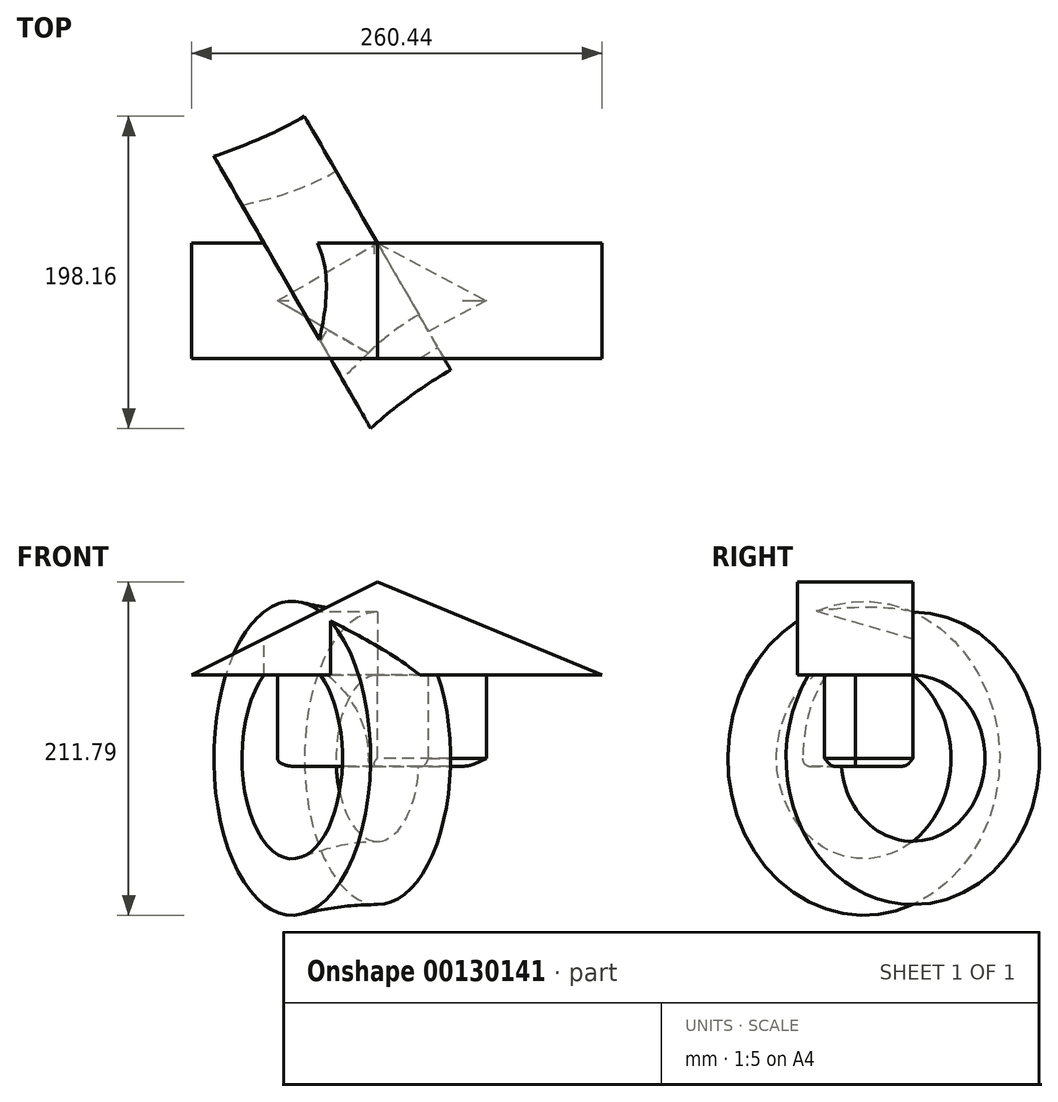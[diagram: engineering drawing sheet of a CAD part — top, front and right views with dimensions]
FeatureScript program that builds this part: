
annotation { "Feature Type Name" : "Feature", "Feature Type Description" : "" }
export const myFeature = defineFeature(function(context is Context, id is Id, definition is map)
    precondition{}
    {
        {
            var Q0;
            Q0=qCreatedBy(makeId("Front.planeOp"),FACE);
            var sketch = newSketch(context, id + "F0", { "sketchPlane" : qUnion([Q0])});
            skLineSegment(sketch, "E0", {"start": v(-118.02, 0) * mm, "end": v(0, 59.3) * mm});
            skLineSegment(sketch, "E1", {"start": v(0, 59.3) * mm, "end": v(142.42, 0) * mm});
            skLineSegment(sketch, "E2", {"start": v(142.42, 0) * mm, "end": v(-118.02, 0) * mm});
            skSolve(sketch);
        }
        {
            var Q0;
            Q0 = qSketchRegion(id + "F0", true);
            extrude(context, id + "F1", {"entities" : qUnion([Q0]), "depth" : 73.24 * mm});
        }
        {
            var Q0;
            Q0=makeQuery(id+"F1.opExtrude","SWEPT_FACE",FACE,{"disambiguationData":[OSD([sQuery(id+"F0.wireOp",EDGE,"E2")])]});
            var sketch = newSketch(context, id + "F2", { "sketchPlane" : qUnion([Q0])});
            skLineSegment(sketch, "E3", {"start": v(0, 73.24) * mm, "end": v(0, 0) * mm});
            skLineSegment(sketch, "E4", {"start": v(0, 0) * mm, "end": v(69.18, 36.62) * mm});
            skPoint(sketch, "E4.endSnap0", {"position": v(0, 36.62) * mm});
            skLineSegment(sketch, "E5", {"start": v(69.18, 36.62) * mm, "end": v(0, 73.24) * mm});
            skLineSegment(sketch, "E6", {"start": v(0, 73.24) * mm, "end": v(-63.56, 36.62) * mm});
            skLineSegment(sketch, "E7", {"start": v(-63.56, 36.62) * mm, "end": v(0, 0) * mm});
            skSolve(sketch);
        }
        {
            var Q0;
            Q0 = qSketchRegion(id + "F2", true);
            extrude(context, id + "F3", {"entities" : qUnion([Q0]), "operationType" : NewBodyOperationType.ADD, "depth" : 57.87 * mm});
        }
        {
            var Q0;
            Q0=makeQuery(id+"F3.opExtrude","CAP_EDGE",EDGE,{"disambiguationData":[OSD([sQuery(id+"F2.wireOp",EDGE,"E4")])],"isStart":false});
            var Q1;
            Q1=makeQuery(id+"F3.opExtrude","CAP_EDGE",EDGE,{"disambiguationData":[OSD([sQuery(id+"F2.wireOp",EDGE,"E5")])],"isStart":false});
            chamfer(context, id + "F4", {"entities" : qUnion([Q0, Q1]), "width" : 5.08 * mm, "tangentPropagation" : true});
        }
        {
            var Q0;
            Q0=makeQuery(id+"F3.opExtrude","CAP_EDGE",EDGE,{"disambiguationData":[OSD([sQuery(id+"F2.wireOp",EDGE,"E6")])],"isStart":false});
            var Q1;
            Q1=makeQuery(id+"F3.opExtrude","CAP_EDGE",EDGE,{"disambiguationData":[OSD([sQuery(id+"F2.wireOp",EDGE,"E7")])],"isStart":false});
            var Q2;
            {var subQ0=sQuery(id+"F2.wireOp",EDGE,"E4");Q2=makeQuery(id+"F4.opChamfer","BLEND_EDGE",EDGE,{"blendedFrom":[makeQuery(id+"F3.opExtrude","CAP_EDGE",EDGE,{"disambiguationData":[OSD([subQ0])],"isStart":false}),makeQuery(id+"F3.opExtrude","CAP_FACE",FACE,{"disambiguationData":[OSD([subQ0,sQuery(id+"F2.wireOp",EDGE,"E5"),sQuery(id+"F2.wireOp",EDGE,"E6"),sQuery(id+"F2.wireOp",EDGE,"E7")])],"isStart":false})],"blendedInto":[makeQuery(id+"F3.opExtrude","CAP_FACE",FACE,{"disambiguationData":[OSD([subQ0,sQuery(id+"F2.wireOp",EDGE,"E5"),sQuery(id+"F2.wireOp",EDGE,"E6"),sQuery(id+"F2.wireOp",EDGE,"E7")])],"isStart":false})]});}
            var Q3;
            {var subQ0=sQuery(id+"F2.wireOp",EDGE,"E5");Q3=makeQuery(id+"F4.opChamfer","BLEND_EDGE",EDGE,{"blendedFrom":[makeQuery(id+"F3.opExtrude","CAP_EDGE",EDGE,{"disambiguationData":[OSD([subQ0])],"isStart":false}),makeQuery(id+"F3.opExtrude","CAP_FACE",FACE,{"disambiguationData":[OSD([sQuery(id+"F2.wireOp",EDGE,"E4"),subQ0,sQuery(id+"F2.wireOp",EDGE,"E6"),sQuery(id+"F2.wireOp",EDGE,"E7")])],"isStart":false})],"blendedInto":[makeQuery(id+"F3.opExtrude","CAP_FACE",FACE,{"disambiguationData":[OSD([sQuery(id+"F2.wireOp",EDGE,"E4"),subQ0,sQuery(id+"F2.wireOp",EDGE,"E6"),sQuery(id+"F2.wireOp",EDGE,"E7")])],"isStart":false})]});}
            fillet(context, id + "F5", {"entities" : qUnion([Q0, Q1, Q2, Q3]), "radius" : 5.08 * mm, "tangentPropagation" : true, "allowEdgeOverflow" : false});
        }
        {
            var Q0;
            Q0=qCreatedBy(makeId("Front.planeOp"),FACE);
            var sketch = newSketch(context, id + "F6", { "sketchPlane" : qUnion([Q0])});
            skLineSegment(sketch, "E8", {"start": v(0, 0) * mm, "end": v(0, 40.17) * mm});
            skLineSegment(sketch, "E9", {"start": v(0, 40.17) * mm, "end": v(-72.17, 40.17) * mm});
            skLineSegment(sketch, "E10", {"start": v(-72.17, 40.17) * mm, "end": v(-72.17, 0) * mm});
            skLineSegment(sketch, "E11", {"start": v(-72.17, 0) * mm, "end": v(0, 0) * mm});
            skLineSegment(sketch, "E12", {"start": v(0, 40.17) * mm, "end": v(0, 0) * mm});
            skSolve(sketch);
        }
        {
            var Q0;
            Q0 = qSketchRegion(id + "F6", true);
            var Q1;
            {var subQ0=sQuery(id+"F2.wireOp",EDGE,"E7");Q1=makeQuery(id+"F5.opFillet","BLEND_EDGE",EDGE,{"blendedFrom":[makeQuery(id+"F3.opExtrude","CAP_EDGE",EDGE,{"disambiguationData":[OSD([subQ0])],"isStart":false}),makeQuery(id+"F3.opExtrude","SWEPT_FACE",FACE,{"disambiguationData":[OSD([subQ0])]})],"blendedInto":[makeQuery(id+"F3.opExtrude","SWEPT_FACE",FACE,{"disambiguationData":[OSD([subQ0])]})]});}
            revolve(context, id + "F7", {"operationType" : NewBodyOperationType.ADD, "entities" : qUnion([Q0]), "axis" : qUnion([Q1]), "revolveType" : RevolveType.FULL});
        }
    });
